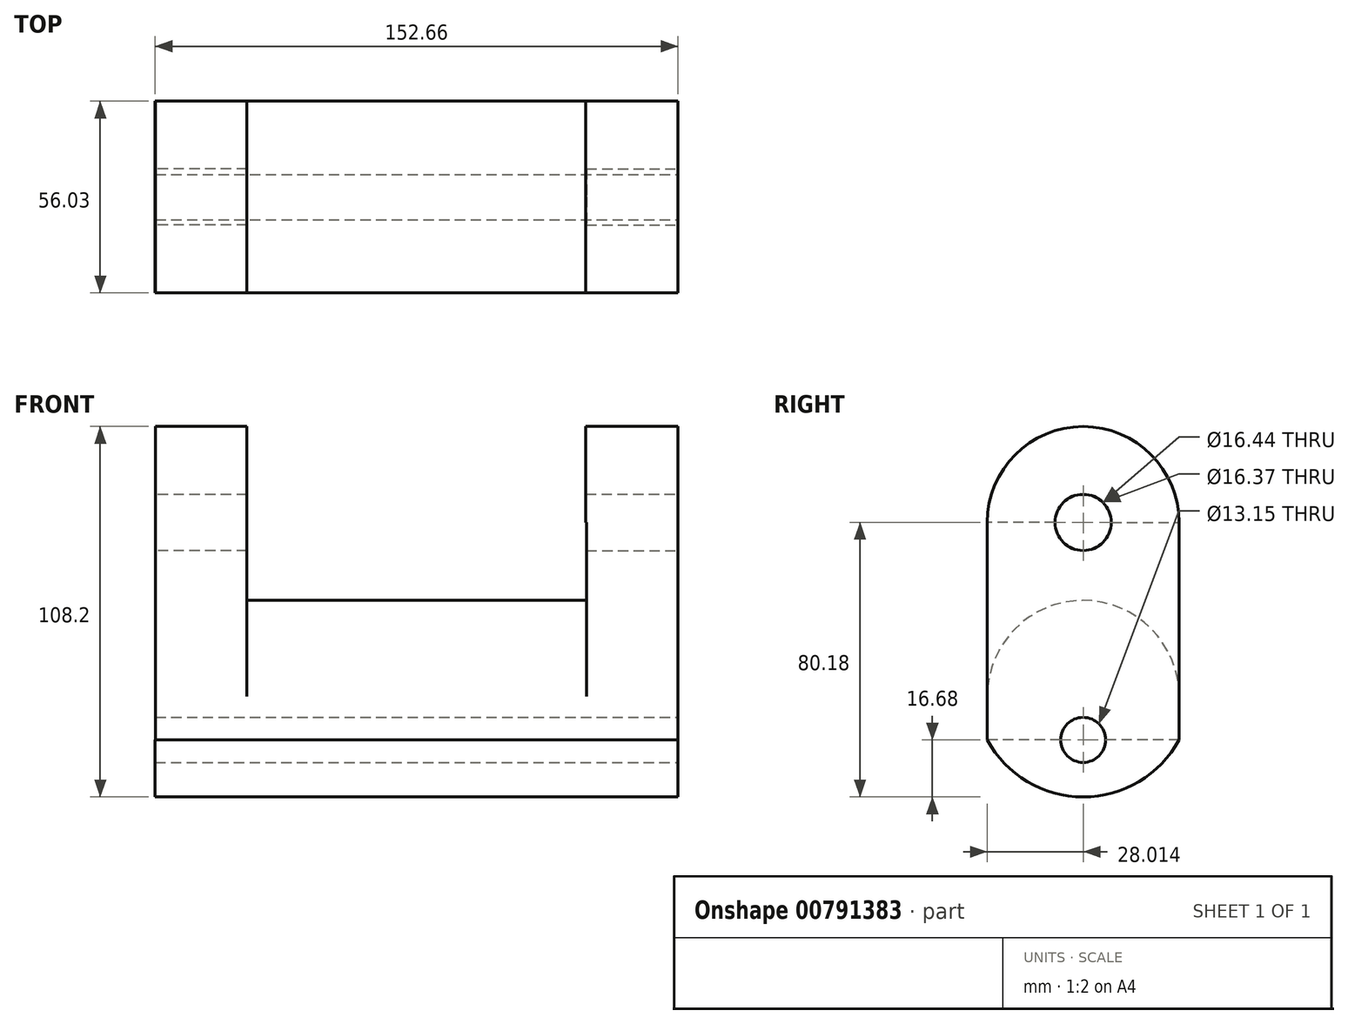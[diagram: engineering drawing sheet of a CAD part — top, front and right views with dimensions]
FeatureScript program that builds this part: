
annotation { "Feature Type Name" : "Feature", "Feature Type Description" : "" }
export const myFeature = defineFeature(function(context is Context, id is Id, definition is map)
    precondition{}
    {
        {
            var Q0;
            Q0=qCreatedBy(makeId("Top.planeOp"),FACE);
            var sketch = newSketch(context, id + "F0", { "sketchPlane" : qUnion([Q0])});
            skLineSegment(sketch, "E0.bottom", {"start": v(-76.03, 0) * mm, "end": v(76.52, 0) * mm});
            skLineSegment(sketch, "E0.top", {"start": v(-76.03, -56.03) * mm, "end": v(76.52, -56.03) * mm});
            skLineSegment(sketch, "E0.left", {"start": v(-76.03, 0) * mm, "end": v(-76.03, -56.03) * mm});
            skLineSegment(sketch, "E0.right", {"start": v(76.52, 0) * mm, "end": v(76.52, -56.03) * mm});
            skSolve(sketch);
        }
        {
            var Q0;
            Q0 = qSketchRegion(id + "F0", true);
            extrude(context, id + "F1", {"entities" : qUnion([Q0]), "depth" : 12.7 * mm, "offsetDistance" : 25.4 * mm});
        }
        {
            var Q0;
            Q0=makeQuery(id+"F1.opExtrude","SWEPT_FACE",FACE,{"disambiguationData":[OSD([sQuery(id+"F0.wireOp",EDGE,"E0.right")])]});
            var sketch = newSketch(context, id + "F2", { "sketchPlane" : qUnion([Q0])});
            skArc(sketch, "E1", {"start": v(-56.03, 0) * mm, "mid": v(-28.02, -16.68) * mm, "end": v(0, 0) * mm});
            skCircle(sketch, "E2", {"center": v(-28.02, 0) * mm, "radius": 6.57 * mm});
            skSolve(sketch);
        }
        {
            var Q0;
            Q0 = qSketchRegion(id + "F2", true);
            var Q1;
            Q1=makeQuery(id+"F2.imprint","IMPRINT",FACE,{"disambiguationData":[TD([[makeQuery(id+"F2.imprint","IMPRINT",EDGE,{"derivedFrom":sQuery(id+"F2.wireOp",EDGE,"E1")}),1.0]])]});
            extrude(context, id + "F3", {"entities" : qUnion([Q0, Q1]), "operationType" : NewBodyOperationType.ADD, "oppositeDirection" : true, "depth" : 152.65 * mm, "offsetDistance" : 25.4 * mm});
        }
        {
            var Q0;
            Q0=makeQuery(id+"F1.opExtrude","CAP_FACE",FACE,{"disambiguationData":[OSD([sQuery(id+"F0.wireOp",EDGE,"E0.bottom"),sQuery(id+"F0.wireOp",EDGE,"E0.top"),sQuery(id+"F0.wireOp",EDGE,"E0.left"),sQuery(id+"F0.wireOp",EDGE,"E0.right")])],"isStart":false});
            var sketch = newSketch(context, id + "F4", { "sketchPlane" : qUnion([Q0])});
            skLineSegment(sketch, "E3.bottom", {"start": v(-76.03, -56.03) * mm, "end": v(-49.36, -56.03) * mm});
            skLineSegment(sketch, "E3.top", {"start": v(-76.03, 0) * mm, "end": v(-49.36, 0) * mm});
            skLineSegment(sketch, "E3.left", {"start": v(-76.03, -56.03) * mm, "end": v(-76.03, 0) * mm});
            skLineSegment(sketch, "E3.right", {"start": v(-49.36, -56.03) * mm, "end": v(-49.36, 0) * mm});
            skLineSegment(sketch, "E4.bottom", {"start": v(76.52, -56.03) * mm, "end": v(49.76, -56.03) * mm});
            skLineSegment(sketch, "E4.top", {"start": v(76.52, 0) * mm, "end": v(49.76, 0) * mm});
            skLineSegment(sketch, "E4.left", {"start": v(76.52, -56.03) * mm, "end": v(76.52, 0) * mm});
            skLineSegment(sketch, "E4.right", {"start": v(49.76, -56.03) * mm, "end": v(49.76, 0) * mm});
            skSolve(sketch);
        }
        {
            var Q0;
            Q0 = qSketchRegion(id + "F4", true);
            extrude(context, id + "F5", {"entities" : qUnion([Q0]), "operationType" : NewBodyOperationType.ADD, "depth" : 50.8 * mm, "offsetDistance" : 25.4 * mm});
        }
        {
            var Q0;
            Q0=makeQuery(id+"F5.opExtrude","SWEPT_FACE",FACE,{"disambiguationData":[OSD([sQuery(id+"F4.wireOp",EDGE,"E3.right")])]});
            var sketch = newSketch(context, id + "F6", { "sketchPlane" : qUnion([Q0])});
            skArc(sketch, "E5", {"start": v(0, 12.7) * mm, "mid": v(-28.02, 40.72) * mm, "end": v(-56.03, 12.7) * mm});
            skSolve(sketch);
        }
        {
            var Q0;
            Q0 = qSketchRegion(id + "F6", true);
            var Q1;
            Q1=makeQuery(id+"F6.imprint","IMPRINT",FACE,{"disambiguationData":[TD([[makeQuery(id+"F6.imprint","IMPRINT",EDGE,{"derivedFrom":sQuery(id+"F6.wireOp",EDGE,"E5")}),1.0]])]});
            extrude(context, id + "F7", {"entities" : qUnion([Q0, Q1]), "operationType" : NewBodyOperationType.ADD, "depth" : 99.31 * mm, "offsetDistance" : 25.4 * mm});
        }
        {
            var Q0;
            {var subQ0=sQuery(id+"F0.wireOp",EDGE,"E0.right");Q0=makeQuery(id+"F5.boolean.opBoolean","MERGE",FACE,{"derivedFrom":[makeQuery(id+"F3.boolean.opBoolean","MERGE",FACE,{"derivedFrom":[makeQuery(id+"F1.opExtrude","SWEPT_FACE",FACE,{"disambiguationData":[OSD([subQ0])]}),makeQuery(id+"F3.opExtrude","CAP_FACE",FACE,{"disambiguationData":[OSD([subQ0,sQuery(id+"F2.wireOp",EDGE,"E1")])],"isStart":true})]}),makeQuery(id+"F5.opExtrude","SWEPT_FACE",FACE,{"disambiguationData":[OSD([sQuery(id+"F4.wireOp",EDGE,"E4.left")])]})]});}
            var sketch = newSketch(context, id + "F8", { "sketchPlane" : qUnion([Q0])});
            skArc(sketch, "E6", {"start": v(0, 63.5) * mm, "mid": v(-28.02, 91.52) * mm, "end": v(-56.03, 63.5) * mm});
            skSolve(sketch);
        }
        {
            var Q0;
            Q0 = qSketchRegion(id + "F8", true);
            var Q1;
            Q1=makeQuery(id+"F8.imprint","IMPRINT",FACE,{"disambiguationData":[TD([[makeQuery(id+"F8.imprint","IMPRINT",EDGE,{"derivedFrom":sQuery(id+"F8.wireOp",EDGE,"E6")}),1.0]])]});
            extrude(context, id + "F9", {"entities" : qUnion([Q0, Q1]), "operationType" : NewBodyOperationType.ADD, "oppositeDirection" : true, "depth" : 26.92 * mm, "offsetDistance" : 25.4 * mm});
        }
        {
            var Q0;
            Q0=makeQuery(id+"F5.boolean.opBoolean","MERGE",FACE,{"derivedFrom":[makeQuery(id+"F1.opExtrude","SWEPT_FACE",FACE,{"disambiguationData":[OSD([sQuery(id+"F0.wireOp",EDGE,"E0.left")])]}),makeQuery(id+"F5.opExtrude","SWEPT_FACE",FACE,{"disambiguationData":[OSD([sQuery(id+"F4.wireOp",EDGE,"E3.left")])]})]});
            var sketch = newSketch(context, id + "F10", { "sketchPlane" : qUnion([Q0])});
            skArc(sketch, "E7", {"start": v(56.03, 63.5) * mm, "mid": v(28.02, 91.52) * mm, "end": v(0, 63.5) * mm});
            skSolve(sketch);
        }
        {
            var Q0;
            Q0 = qSketchRegion(id + "F10", true);
            var Q1;
            Q1=makeQuery(id+"F10.imprint","IMPRINT",FACE,{"disambiguationData":[TD([[makeQuery(id+"F10.imprint","IMPRINT",EDGE,{"derivedFrom":sQuery(id+"F10.wireOp",EDGE,"E7")}),1.0]])]});
            extrude(context, id + "F11", {"entities" : qUnion([Q0, Q1]), "operationType" : NewBodyOperationType.ADD, "oppositeDirection" : true, "depth" : 26.67 * mm, "offsetDistance" : 25.4 * mm});
        }
        {
            var Q0;
            {var subQ0=sQuery(id+"F4.wireOp",EDGE,"E4.left");var subQ1=sQuery(id+"F0.wireOp",EDGE,"E0.right");Q0=makeQuery(id+"F9.boolean.opBoolean","MERGE",FACE,{"derivedFrom":[makeQuery(id+"F5.boolean.opBoolean","MERGE",FACE,{"derivedFrom":[makeQuery(id+"F3.boolean.opBoolean","MERGE",FACE,{"derivedFrom":[makeQuery(id+"F1.opExtrude","SWEPT_FACE",FACE,{"disambiguationData":[OSD([subQ1])]}),makeQuery(id+"F3.opExtrude","CAP_FACE",FACE,{"disambiguationData":[OSD([subQ1,sQuery(id+"F2.wireOp",EDGE,"E1")])],"isStart":true})]}),makeQuery(id+"F5.opExtrude","SWEPT_FACE",FACE,{"disambiguationData":[OSD([subQ0])]})]}),makeQuery(id+"F9.opExtrude","CAP_FACE",FACE,{"disambiguationData":[OSD([subQ0,sQuery(id+"F8.wireOp",EDGE,"E6")])],"isStart":true})]});}
            var sketch = newSketch(context, id + "F12", { "sketchPlane" : qUnion([Q0])});
            skLineSegment(sketch, "E8", {"start": v(-56.03, 63.5) * mm, "end": v(0, 63.5) * mm});
            skCircle(sketch, "E9", {"center": v(-28.02, 63.5) * mm, "radius": 8.22 * mm});
            skSolve(sketch);
        }
        {
            var Q0;
            {var subQ0=sQuery(id+"F12.wireOp",EDGE,"E9");var subQ1=sQuery(id+"F12.wireOp",EDGE,"E8");var subQ2=makeQuery(id+"F12.imprint","INTERSECT",VERTEX,{"disambiguationData":[OD(0.0)],"derivedFrom":[subQ1,subQ0]});Q0=makeQuery(id+"F12.imprint","IMPRINT",FACE,{"disambiguationData":[TD([[makeQuery(id+"F12.imprint","IMPRINT",EDGE,{"disambiguationData":[TD([[subQ2,-1.0]])],"derivedFrom":subQ1}),1.0]])]});}
            var Q1;
            {var subQ0=sQuery(id+"F12.wireOp",EDGE,"E9");var subQ1=sQuery(id+"F12.wireOp",EDGE,"E8");var subQ2=makeQuery(id+"F12.imprint","INTERSECT",VERTEX,{"disambiguationData":[OD(0.0)],"derivedFrom":[subQ1,subQ0]});Q1=makeQuery(id+"F12.imprint","IMPRINT",FACE,{"disambiguationData":[TD([[makeQuery(id+"F12.imprint","IMPRINT",EDGE,{"disambiguationData":[TD([[subQ2,-1.0]])],"derivedFrom":subQ1}),-1.0]])]});}
            extrude(context, id + "F13", {"entities" : qUnion([Q0, Q1]), "operationType" : NewBodyOperationType.REMOVE, "oppositeDirection" : true, "depth" : 36.32 * mm, "offsetDistance" : 25.4 * mm});
        }
        {
            var Q0;
            {var subQ0=sQuery(id+"F4.wireOp",EDGE,"E3.left");Q0=makeQuery(id+"F11.boolean.opBoolean","MERGE",FACE,{"derivedFrom":[makeQuery(id+"F5.boolean.opBoolean","MERGE",FACE,{"derivedFrom":[makeQuery(id+"F1.opExtrude","SWEPT_FACE",FACE,{"disambiguationData":[OSD([sQuery(id+"F0.wireOp",EDGE,"E0.left")])]}),makeQuery(id+"F5.opExtrude","SWEPT_FACE",FACE,{"disambiguationData":[OSD([subQ0])]})]}),makeQuery(id+"F11.opExtrude","CAP_FACE",FACE,{"disambiguationData":[OSD([subQ0,sQuery(id+"F10.wireOp",EDGE,"E7")])],"isStart":true})]});}
            var sketch = newSketch(context, id + "F14", { "sketchPlane" : qUnion([Q0])});
            skLineSegment(sketch, "E10", {"start": v(0, 63.5) * mm, "end": v(56.03, 63.5) * mm});
            skCircle(sketch, "E11", {"center": v(28.02, 63.5) * mm, "radius": 8.19 * mm});
            skSolve(sketch);
        }
        {
            var Q0;
            {var subQ0=sQuery(id+"F14.wireOp",EDGE,"E11");var subQ1=sQuery(id+"F14.wireOp",EDGE,"E10");var subQ2=makeQuery(id+"F14.imprint","INTERSECT",VERTEX,{"disambiguationData":[OD(0.0)],"derivedFrom":[subQ1,subQ0]});Q0=makeQuery(id+"F14.imprint","IMPRINT",FACE,{"disambiguationData":[TD([[makeQuery(id+"F14.imprint","IMPRINT",EDGE,{"disambiguationData":[TD([[subQ2,-1.0]])],"derivedFrom":subQ1}),-1.0]])]});}
            var Q1;
            {var subQ0=sQuery(id+"F14.wireOp",EDGE,"E11");var subQ1=sQuery(id+"F14.wireOp",EDGE,"E10");var subQ2=makeQuery(id+"F14.imprint","INTERSECT",VERTEX,{"disambiguationData":[OD(0.0)],"derivedFrom":[subQ1,subQ0]});Q1=makeQuery(id+"F14.imprint","IMPRINT",FACE,{"disambiguationData":[TD([[makeQuery(id+"F14.imprint","IMPRINT",EDGE,{"disambiguationData":[TD([[subQ2,-1.0]])],"derivedFrom":subQ1}),1.0]])]});}
            extrude(context, id + "F15", {"entities" : qUnion([Q0, Q1]), "operationType" : NewBodyOperationType.REMOVE, "oppositeDirection" : true, "depth" : 44.45 * mm, "offsetDistance" : 25.4 * mm});
        }
        {
            var Q0;
            Q0 = qSketchRegion(id + "F2", true);
            extrude(context, id + "F16", {"entities" : qUnion([Q0]), "operationType" : NewBodyOperationType.REMOVE, "oppositeDirection" : true, "depth" : 188.21 * mm, "offsetDistance" : 25.4 * mm});
        }
    });
